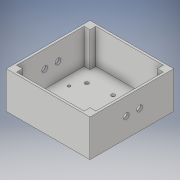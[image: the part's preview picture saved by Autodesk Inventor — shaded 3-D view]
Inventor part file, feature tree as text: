
AUTODESK INVENTOR PART (.ipt)
format: ipt  version: 2018 (Build 220112000, 112)  size: 184,832 bytes
history: native  units: in
note: dims shown in document units (in); Inventor stores cm internally (conversion verified against a paired STEP export)
features: extrude x5, sketch x5
ambient origin geometry x8: Origin, YZ Plane, XZ Plane, XY Plane, X Axis, Y Axis, Z Axis, Center Point
bodies: Solid1 (feature_tree)
feature tree (10):
  extrude  "Extrusion1"  Depth=3.621in
  extrude  "Extrusion2"  Depth=3.425in
  extrude  "Extrusion3"  Depth=0.354in
  extrude  "Extrusion4"  Depth=0.354in
  extrude  "Extrusion5"  Depth=1.496in TaperAngle=0.0deg
  sketch  "Sketch1"  dims[d0=3.621in d1=3.621in]
  sketch  "Sketch2"  dims[d2=0.098in d3=0.0in d4=3.425in]
  sketch  "Sketch3"  dims[d5=3.425in d6=0.354in]
  sketch  "Sketch4"  dims[d7=0.354in d10=0.354in]
  sketch  "Sketch5"  dims[d11=0.354in d14=1.496in d15=0.0in d16=2.047in d17=1.772in d18=0.157in d19=0.157in d20=0.157in d21=0.157in d22=2.598in d23=0.787in d24=0.118in d25=0.118in d26=0.118in d27=0.118in d30=0.164in d31=0.164in d32=0.0in d33=0.0in d37=0.0in d38=0.0in d42=0.0in d43=0.0in d44=0.374in d45=0.0in d46=0.837in d47=0.578in d48=0.25in d49=0.25in d50=0.374in d51=0.837in d52=0.578in d53=0.25in d54=0.25in]
